# Revit family: PAYE S7 4M
name_source: partatom
category: Lighting Fixtures
revit_build: Autodesk Revit 2017 (Build: 20160225_1515(x64)
units: mm (PartAtom-declared; Revit-internal decimal feet)

## family parameters
Cut with Voids When Loaded = No
Host = Face
Light Source = Yes
Part Type = Normal
Room Calculation Point = No
Round Connector Dimension = Use Diameter
Shared = No

## types (3) — shared parameters
Body Material = IRON
Color Filter = 16777215
Default Elevation = 122 cm
Dimming Lamp Color Temperature Shift = <None>
Emit from Line Length = 61 cm
Flicker = Free Flicker
Height = 400 cm
IP = IP65
Lamp = LED
Manufacturer = SHOA
Model = PAYE S7-4m
Photometric Web File = 8012-36w-3000k.ies
Protection Class = Class I
Tilt Angle = 90.00°
Type medule = POWER LED
Voltage/Frequency = 230v/50hz
Wattage. = 12 W
Width = 133 cm
consumption current = 0 A
website = www.shoaco.com

## per-type parameters (varying)
| type | body color |
| PAYE S7-4m(White color-3000K-LED) | White Body |
| PAYE S7-4m(Gray color-3000K-LED) | Gray color |
| PAYE S7-4m(Black color-3000K-LED) | Black Body |

## geometry (parser evidence)
native form markers: Sweep x3
no freeform markers — native parametric forms only
